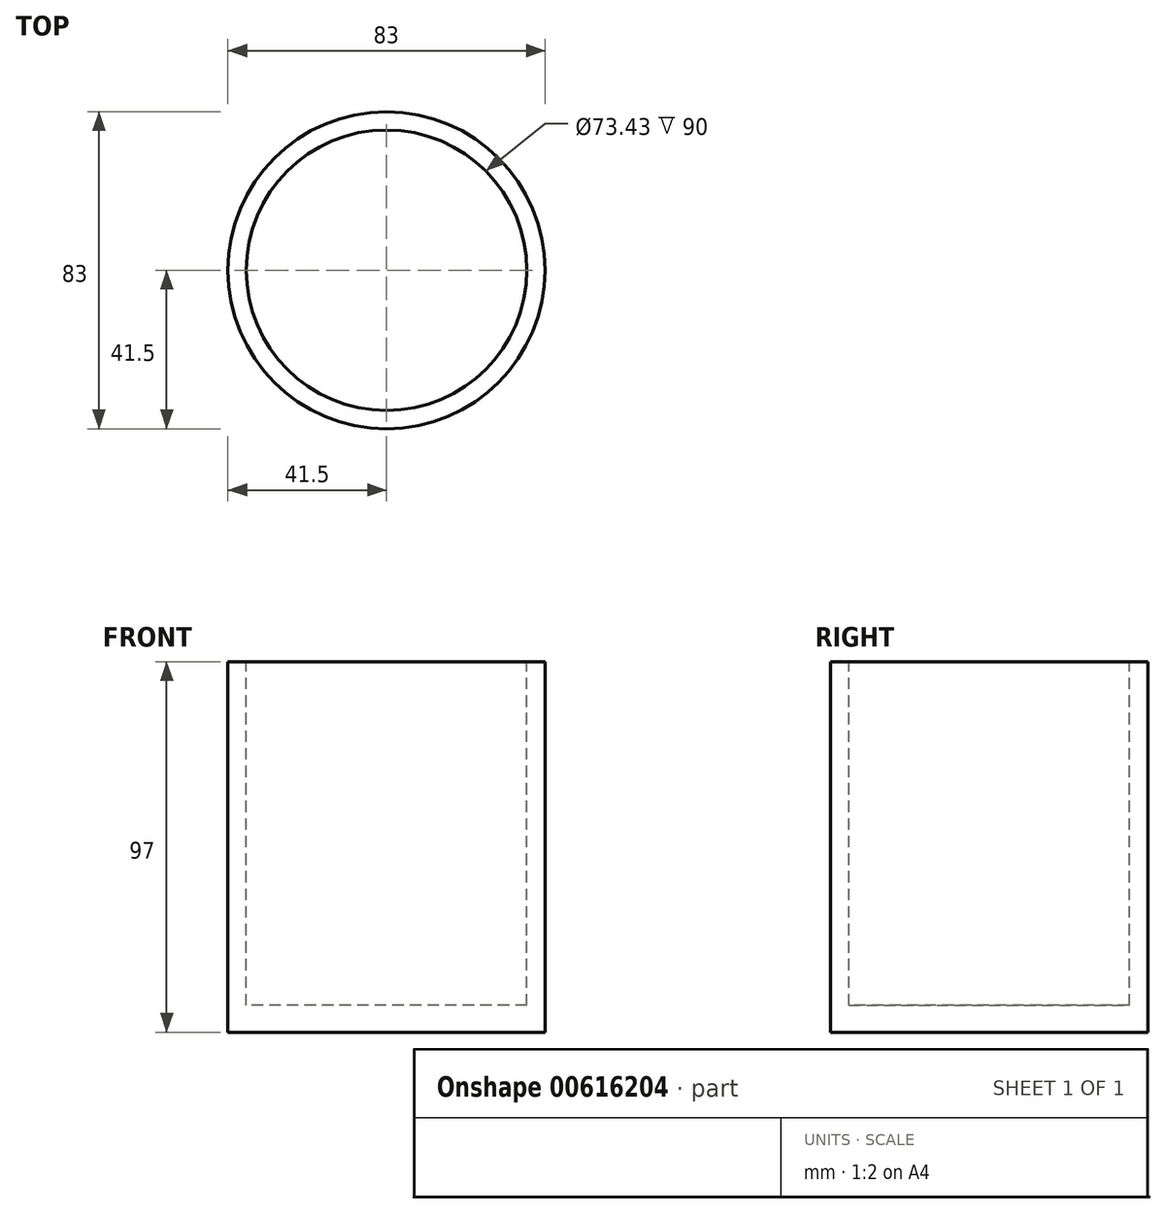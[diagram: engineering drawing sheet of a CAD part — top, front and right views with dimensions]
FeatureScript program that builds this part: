
annotation { "Feature Type Name" : "Feature", "Feature Type Description" : "" }
export const myFeature = defineFeature(function(context is Context, id is Id, definition is map)
    precondition{}
    {
        {
            var Q0;
            Q0=qCreatedBy(makeId("Top.planeOp"),FACE);
            var sketch = newSketch(context, id + "F0", { "sketchPlane" : qUnion([Q0])});
            skCircle(sketch, "E0", {"center": v(0, 0) * mm, "radius": 41.5 * mm});
            skSolve(sketch);
        }
        {
            var Q0;
            Q0=makeQuery(id+"F0.imprint","IMPRINT",FACE,{"disambiguationData":[TD([[makeQuery(id+"F0.imprint","IMPRINT",EDGE,{"derivedFrom":sQuery(id+"F0.wireOp",EDGE,"E0")}),1.0]])]});
            extrude(context, id + "F1", {"entities" : qUnion([Q0]), "depth" : 97 * mm, "offsetDistance" : 25 * mm});
        }
        {
            var Q0;
            Q0=qCreatedBy(makeId("Right.planeOp"),FACE);
            var sketch = newSketch(context, id + "F2", { "sketchPlane" : qUnion([Q0])});
            skFitSpline(sketch, "E1", {"points": [v(23.26, 74.84) * mm, v(48.72, 75.71) * mm, v(59.25, 67.37) * mm, v(65.4, 48.94) * mm, v(64.52, 25.68) * mm, v(55.74, 13.39) * mm, v(44.33, 10.31) * mm, v(25.46, 10.31) * mm], "startDerivative": vector(166.32, 23.63) * mm, "endDerivative": vector(-136.2, 3.76) * mm});
            skSolve(sketch);
        }
        {
            var Q0;
            Q0=qCreatedBy(makeId("Front.planeOp"),FACE);
            cPlane(context, id + "F3", {"entities" : qUnion([Q0]), "cplaneType" : CPlaneType.OFFSET, "offset" : 35 * mm, "oppositeDirection" : true, "width" : 150 * mm, "height" : 150 * mm});
        }
        {
            var Q0;
            Q0=qCreatedBy(id+"F3.planeOp",FACE);
            var sketch = newSketch(context, id + "F4", { "sketchPlane" : qUnion([Q0])});
            skCircle(sketch, "E2", {"center": v(0, 69.75) * mm, "radius": 6.69 * mm});
            skSolve(sketch);
        }
        {
            var Q0;
            Q0=makeQuery(id+"F1.opExtrude","CAP_FACE",FACE,{"disambiguationData":[OSD([sQuery(id+"F0.wireOp",EDGE,"E0")])],"isStart":false});
            var sketch = newSketch(context, id + "F5", { "sketchPlane" : qUnion([Q0])});
            skCircle(sketch, "E3", {"center": v(0, 0) * mm, "radius": 36.71 * mm});
            skSolve(sketch);
        }
        {
            var Q0;
            Q0=makeQuery(id+"F5.imprint","IMPRINT",FACE,{"disambiguationData":[TD([[makeQuery(id+"F5.imprint","IMPRINT",EDGE,{"derivedFrom":sQuery(id+"F5.wireOp",EDGE,"E3")}),1.0]])]});
            extrude(context, id + "F6", {"entities" : qUnion([Q0]), "operationType" : NewBodyOperationType.REMOVE, "oppositeDirection" : true, "depth" : 90 * mm, "offsetDistance" : 25 * mm});
        }
    });
